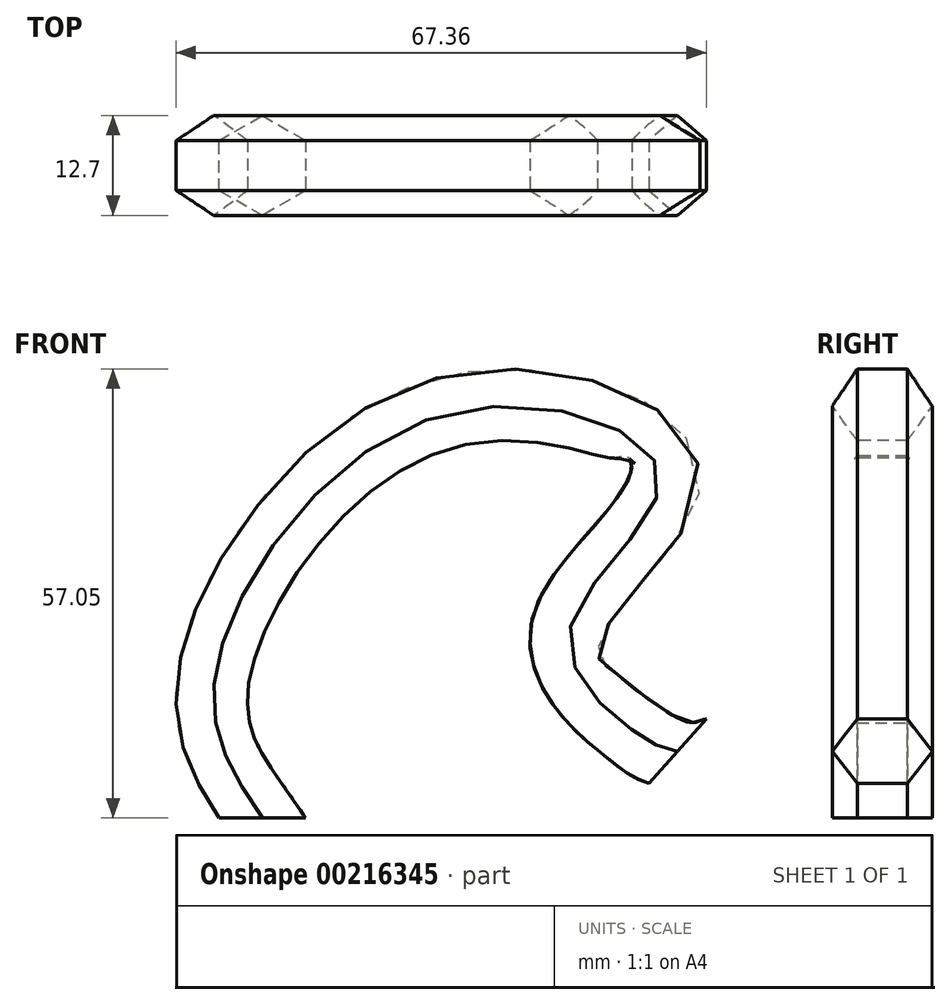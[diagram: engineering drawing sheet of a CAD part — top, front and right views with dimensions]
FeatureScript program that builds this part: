
annotation { "Feature Type Name" : "Feature", "Feature Type Description" : "" }
export const myFeature = defineFeature(function(context is Context, id is Id, definition is map)
    precondition{}
    {
        {
            var Q0;
            Q0=qCreatedBy(makeId("Top.planeOp"),FACE);
            var sketch = newSketch(context, id + "F0", { "sketchPlane" : qUnion([Q0])});
            skCircle(sketch, "E0.cCircle", {"center": v(0, 0) * mm, "radius": 5.5 * mm, "construction": true});
            skLineSegment(sketch, "E0.0", {"start": v(-5.5, 3.18) * mm, "end": v(0, 6.35) * mm});
            skLineSegment(sketch, "E0.1", {"start": v(0, 6.35) * mm, "end": v(5.5, 3.18) * mm});
            skLineSegment(sketch, "E0.2", {"start": v(5.5, 3.18) * mm, "end": v(5.5, -3.17) * mm});
            skLineSegment(sketch, "E0.3", {"start": v(5.5, -3.18) * mm, "end": v(0, -6.35) * mm});
            skLineSegment(sketch, "E0.4", {"start": v(0, -6.35) * mm, "end": v(-5.5, -3.18) * mm});
            skLineSegment(sketch, "E0.5", {"start": v(-5.5, -3.17) * mm, "end": v(-5.5, 3.18) * mm});
            skPoint(sketch, "E0.0.midPoint", {"position": v(-2.75, 4.76) * mm});
            skSolve(sketch);
        }
        {
            var Q0;
            Q0=qCreatedBy(makeId("Front.planeOp"),FACE);
            var sketch = newSketch(context, id + "F1", { "sketchPlane" : qUnion([Q0])});
            skFitSpline(sketch, "E1", {"points": [v(0, 0) * mm, v(-5.66, 10.88) * mm, v(-3.28, 26.67) * mm, v(24.73, 51.7) * mm, v(50.51, 43.23) * mm, v(39, 23.64) * mm, v(47.38, 10.88) * mm, v(52.74, 8.5) * mm], "startDerivative": vector(-60.99, 90.95) * mm, "endDerivative": vector(69.25, -9.32) * mm});
            skSolve(sketch);
        }
        {
            var Q0;
            Q0 = qSketchRegion(id + "F0", true);
            var Q1;
            Q1 = qConstructionFilter(qBodyType(qCreatedBy(id + "F1" ,EDGE), BodyType.WIRE), ConstructionObject.NO);
            sweep(context, id + "F2", {"profiles" : qUnion([Q0]), "path" : qUnion([Q1])});
        }
    });
